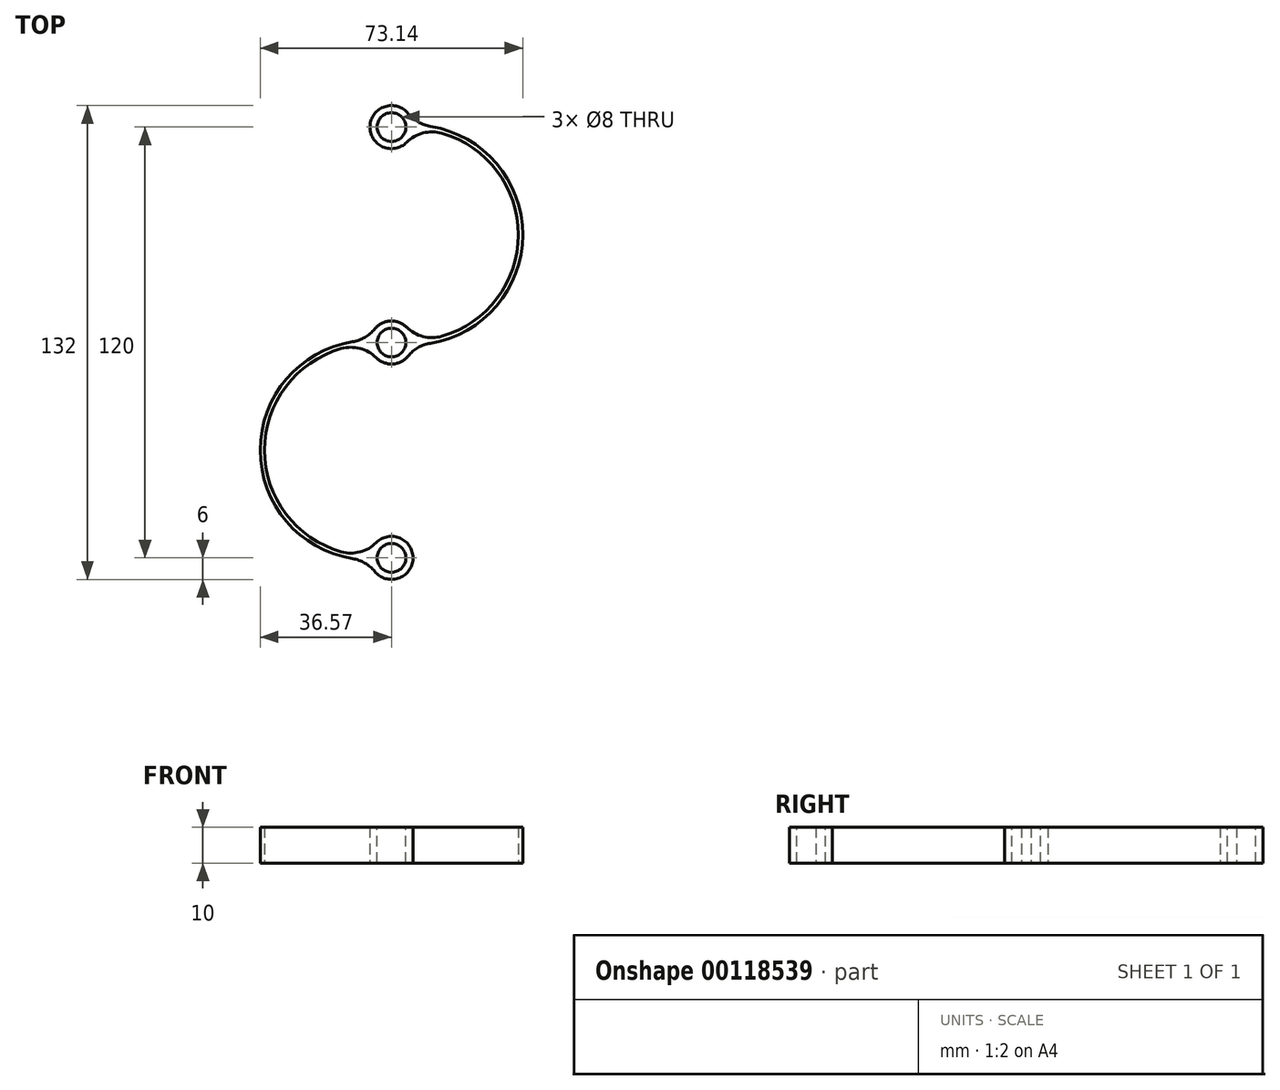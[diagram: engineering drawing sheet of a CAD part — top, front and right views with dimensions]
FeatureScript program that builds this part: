
annotation { "Feature Type Name" : "Feature", "Feature Type Description" : "" }
export const myFeature = defineFeature(function(context is Context, id is Id, definition is map)
    precondition{}
    {
        {
            var Q0;
            Q0=qCreatedBy(makeId("Top.planeOp"),FACE);
            var sketch = newSketch(context, id + "F0", { "sketchPlane" : qUnion([Q0])});
            skCircle(sketch, "E0", {"center": v(0, 60) * mm, "radius": 6 * mm});
            skCircle(sketch, "E1", {"center": v(0, 0) * mm, "radius": 6 * mm});
            skArc(sketch, "E2", {"start": v(5.97, -0.6) * mm, "mid": v(36.57, 30) * mm, "end": v(5.97, 60.6) * mm});
            skArc(sketch, "E3", {"start": v(5.97, 0.6) * mm, "mid": v(35.37, 30) * mm, "end": v(5.97, 59.4) * mm});
            skLineSegment(sketch, "E4", {"start": v(5.97, -9.97) * mm, "end": v(5.97, 85) * mm, "construction": true});
            skCircle(sketch, "E5", {"center": v(0, -60) * mm, "radius": 6 * mm});
            skArc(sketch, "E6", {"start": v(-5.97, 0.6) * mm, "mid": v(-36.57, -30) * mm, "end": v(-5.97, -60.6) * mm});
            skArc(sketch, "E7", {"start": v(-5.97, -0.6) * mm, "mid": v(-35.37, -30) * mm, "end": v(-5.97, -59.4) * mm});
            skLineSegment(sketch, "E8", {"start": v(-5.97, -94.18) * mm, "end": v(-5.97, 26.02) * mm, "construction": true});
            skSolve(sketch);
        }
        {
            var Q0;
            {var subQ0=sQuery(id+"F0.wireOp",EDGE,"E0");var subQ1=makeQuery(id+"F0.imprint","INTERSECT",VERTEX,{"derivedFrom":[subQ0,sQuery(id+"F0.wireOp",EDGE,"E2")]});Q0=makeQuery(id+"F0.imprint","IMPRINT",FACE,{"disambiguationData":[TD([[makeQuery(id+"F0.imprint","IMPRINT",EDGE,{"disambiguationData":[TD([[subQ1,-1.0]])],"derivedFrom":subQ0}),1.0]])]});}
            var Q1;
            {var subQ0=sQuery(id+"F0.wireOp",EDGE,"E2");Q1=makeQuery(id+"F0.imprint","IMPRINT",FACE,{"disambiguationData":[TD([[makeQuery(id+"F0.imprint","IMPRINT",EDGE,{"derivedFrom":subQ0}),1.0]])]});}
            var Q2;
            {var subQ0=sQuery(id+"F0.wireOp",EDGE,"E1");var subQ1=makeQuery(id+"F0.imprint","INTERSECT",VERTEX,{"derivedFrom":[subQ0,sQuery(id+"F0.wireOp",EDGE,"E2")]});Q2=makeQuery(id+"F0.imprint","IMPRINT",FACE,{"disambiguationData":[TD([[makeQuery(id+"F0.imprint","IMPRINT",EDGE,{"disambiguationData":[TD([[subQ1,1.0]])],"derivedFrom":subQ0}),1.0]])]});}
            var Q3;
            {var subQ0=sQuery(id+"F0.wireOp",EDGE,"E6");Q3=makeQuery(id+"F0.imprint","IMPRINT",FACE,{"disambiguationData":[TD([[makeQuery(id+"F0.imprint","IMPRINT",EDGE,{"derivedFrom":subQ0}),1.0]])]});}
            var Q4;
            {var subQ0=sQuery(id+"F0.wireOp",EDGE,"E5");var subQ1=makeQuery(id+"F0.imprint","INTERSECT",VERTEX,{"derivedFrom":[subQ0,sQuery(id+"F0.wireOp",EDGE,"E6")]});Q4=makeQuery(id+"F0.imprint","IMPRINT",FACE,{"disambiguationData":[TD([[makeQuery(id+"F0.imprint","IMPRINT",EDGE,{"disambiguationData":[TD([[subQ1,1.0]])],"derivedFrom":subQ0}),1.0]])]});}
            extrude(context, id + "F1", {"entities" : qUnion([Q0, Q1, Q2, Q3, Q4]), "depth" : 10 * mm});
        }
        {
            var Q0;
            Q0=makeQuery(id+"F1.opExtrude","SWEPT_EDGE",EDGE,{"disambiguationData":[OSD([sQuery(id+"F0.wireOp",EDGE,"E1"),sQuery(id+"F0.wireOp",EDGE,"E2")])]});
            var Q1;
            Q1=makeQuery(id+"F1.opExtrude","SWEPT_EDGE",EDGE,{"disambiguationData":[OSD([sQuery(id+"F0.wireOp",EDGE,"E0"),sQuery(id+"F0.wireOp",EDGE,"E3")])]});
            var Q2;
            Q2=makeQuery(id+"F1.opExtrude","SWEPT_EDGE",EDGE,{"disambiguationData":[OSD([sQuery(id+"F0.wireOp",EDGE,"E1"),sQuery(id+"F0.wireOp",EDGE,"E3")])]});
            var Q3;
            Q3=makeQuery(id+"F1.opExtrude","SWEPT_EDGE",EDGE,{"disambiguationData":[OSD([sQuery(id+"F0.wireOp",EDGE,"E0"),sQuery(id+"F0.wireOp",EDGE,"E2")])]});
            var Q4;
            Q4=makeQuery(id+"F1.opExtrude","SWEPT_EDGE",EDGE,{"disambiguationData":[OSD([sQuery(id+"F0.wireOp",EDGE,"E5"),sQuery(id+"F0.wireOp",EDGE,"E6")])]});
            var Q5;
            Q5=makeQuery(id+"F1.opExtrude","SWEPT_EDGE",EDGE,{"disambiguationData":[OSD([sQuery(id+"F0.wireOp",EDGE,"E1"),sQuery(id+"F0.wireOp",EDGE,"E7")])]});
            var Q6;
            Q6=makeQuery(id+"F1.opExtrude","SWEPT_EDGE",EDGE,{"disambiguationData":[OSD([sQuery(id+"F0.wireOp",EDGE,"E5"),sQuery(id+"F0.wireOp",EDGE,"E7")])]});
            var Q7;
            Q7=makeQuery(id+"F1.opExtrude","SWEPT_EDGE",EDGE,{"disambiguationData":[OSD([sQuery(id+"F0.wireOp",EDGE,"E1"),sQuery(id+"F0.wireOp",EDGE,"E6")])]});
            fillet(context, id + "F2", {"entities" : qUnion([Q0, Q1, Q2, Q3, Q4, Q5, Q6, Q7]), "radius" : 10 * mm, "tangentPropagation" : true, "allowEdgeOverflow" : false});
        }
        {
            var Q0;
            Q0=makeQuery(id+"F1.opExtrude","CAP_FACE",FACE,{"disambiguationData":[OSD([sQuery(id+"F0.wireOp",EDGE,"E0"),sQuery(id+"F0.wireOp",EDGE,"E1"),sQuery(id+"F0.wireOp",EDGE,"E2"),sQuery(id+"F0.wireOp",EDGE,"E3")])],"isStart":false});
            var sketch = newSketch(context, id + "F3", { "sketchPlane" : qUnion([Q0])});
            skCircle(sketch, "E9", {"center": v(0, 0) * mm, "radius": 4 * mm});
            skCircle(sketch, "E10", {"center": v(0, 60) * mm, "radius": 4 * mm});
            skCircle(sketch, "E11", {"center": v(0, -60) * mm, "radius": 4 * mm});
            skSolve(sketch);
        }
        {
            var Q0;
            Q0 = qSketchRegion(id + "F3", true);
            extrude(context, id + "F4", {"entities" : qUnion([Q0]), "operationType" : NewBodyOperationType.REMOVE, "endBound" : BoundingType.UP_TO_NEXT, "oppositeDirection" : true, "depth" : 25.4 * mm});
        }
    });
